# Revit family: Plumbing_Pipes_Aignep_Safety-Kit-for-90806-90808
name_source: partatom
category: Pipe Accessories
revit_build: Autodesk Revit 2018 (Build: 20170223_1515(x64)
units: mm (PartAtom-declared; Revit-internal decimal feet)

## family parameters
Cut with Voids When Loaded = No
OmniClass Number = 23.27.43.00
OmniClass Title = Pipe Fittings
Part Type = Normal
Round Connector Dimension = Use Diameter
Shared = No

## types (1)
- 90808
    Article Code = 90808 00 001
    Assembly Code = D2040100
    BIMobject category = Joints
    Description = Safety kit for 90806
    Design country = Italy
    Edition number = 1
    IFC Classification = Pipe Fitting
    Keynote = 15410
    Manufacturer = Aignep Spa
    Manufacturer country = Italy
    Manufacturer name = Aignep Spa
    Material main = Steel
    Model = 90808
    OmniClass Code = 23-27 43 00
    OmniClass Description = Pipe Fittings
    Product Guid = e5c345e9-7fa7-4b49-a057-3c7c8c6dd7ff
    Product Material = AIGNEP - Aluminium - Grey
    Product SKU = Safety-Kit-For-90806-90808
    Product certification = https://www.aignep.com
    Product data url = https://www.bimobject.com
    Product family = INFINITY
    Product group = Fittings
    Product name = Safety Kit For 90806 - 90808
    Product url = https://www.aignep.com
    QR code = https://www.bimobject.com
    URL = https://www.aignep.com

## geometry (parser evidence)
native form markers: Sweep x2
no freeform markers — native parametric forms only
